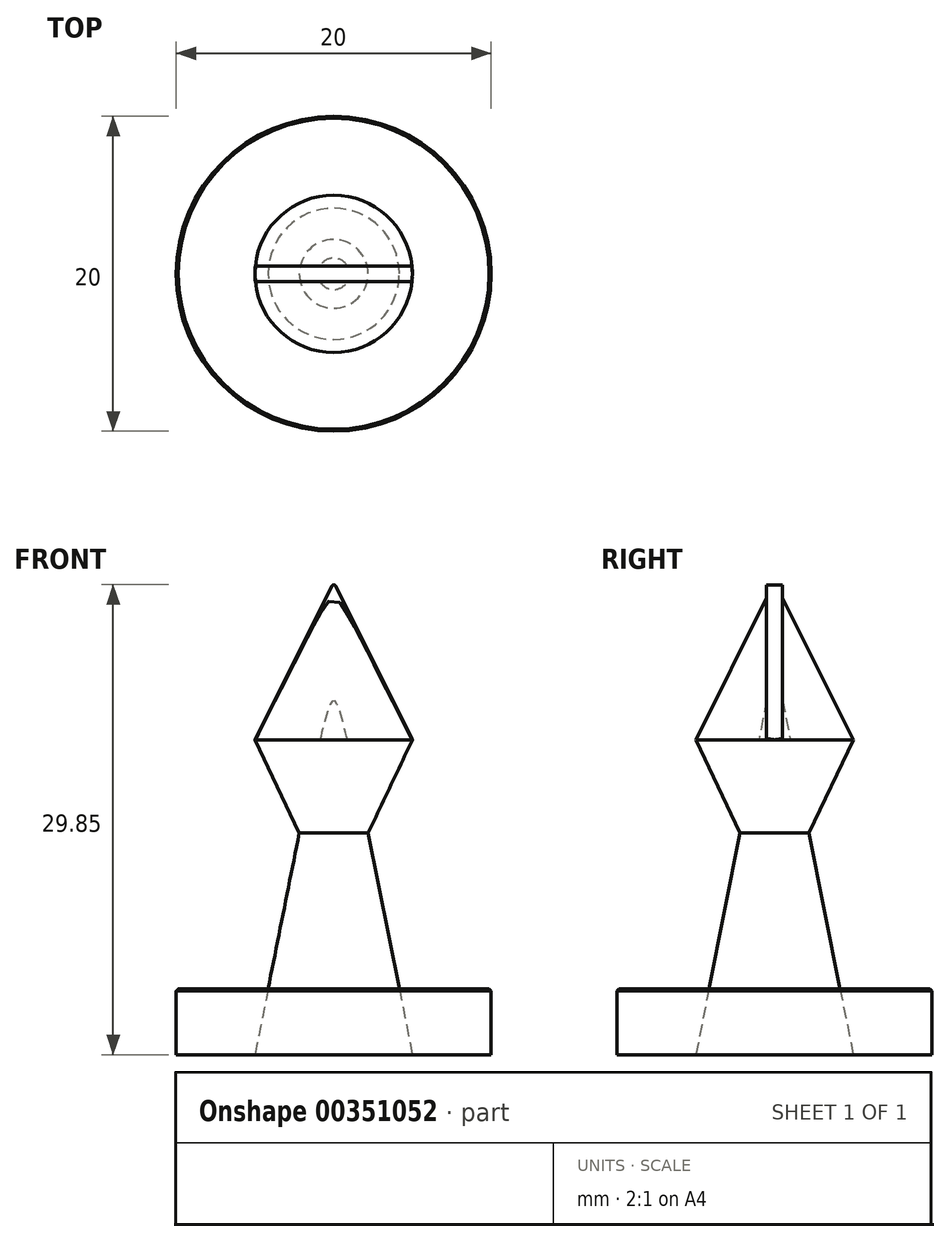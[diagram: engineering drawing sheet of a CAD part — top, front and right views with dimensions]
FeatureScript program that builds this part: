
annotation { "Feature Type Name" : "Feature", "Feature Type Description" : "" }
export const myFeature = defineFeature(function(context is Context, id is Id, definition is map)
    precondition{}
    {
        {
            assignVariable(context, id + "F0", {"name" : "H", "anyValue" : 1});
        }
        {
            assignVariable(context, id + "F1", {"name" : "W", "anyValue" : .5});
        }
        {
            var Q0;
            Q0=qCreatedBy(makeId("Front.planeOp"),FACE);
            var sketch = newSketch(context, id + "F2", { "sketchPlane" : qUnion([Q0])});
            skLineSegment(sketch, "E0", {"start": v(0, 0) * mm, "end": v(0, 30) * mm});
            skPoint(sketch, "E1", {"position": v(0, 20) * mm});
            skPoint(sketch, "E2", {"position": v(0, 25) * mm});
            skLineSegment(sketch, "E3", {"start": v(0, 0) * mm, "end": v(-5, 0) * mm});
            skLineSegment(sketch, "E4", {"start": v(0, 25) * mm, "end": v(-5, 0) * mm});
            skLineSegment(sketch, "E5.bottom", {"start": v(0, 0) * mm, "end": v(-10, 0) * mm});
            skLineSegment(sketch, "E5.top", {"start": v(0, 4.17) * mm, "end": v(-10, 4.17) * mm});
            skLineSegment(sketch, "E5.left", {"start": v(0, 0) * mm, "end": v(0, 4.17) * mm});
            skLineSegment(sketch, "E5.right", {"start": v(-10, 0) * mm, "end": v(-10, 4.17) * mm});
            skLineSegment(sketch, "E6.bottom", {"start": v(-5, 30) * mm, "end": v(5, 30) * mm});
            skLineSegment(sketch, "E6.top", {"start": v(-5, 20) * mm, "end": v(5, 20) * mm});
            skLineSegment(sketch, "E6.left", {"start": v(-5, 30) * mm, "end": v(-5, 20) * mm});
            skLineSegment(sketch, "E6.right", {"start": v(5, 30) * mm, "end": v(5, 20) * mm});
            skLineSegment(sketch, "E7", {"start": v(0, 30) * mm, "end": v(-5, 20) * mm});
            skLineSegment(sketch, "E8", {"start": v(0, 30) * mm, "end": v(5, 20) * mm});
            skLineSegment(sketch, "E9", {"start": v(-5, 20) * mm, "end": v(-2.19, 14.07) * mm});
            skSolve(sketch);
        }
        {
            var Q0;
            {var subQ5=sQuery(id+"F2.wireOp",EDGE,"E5.right");Q0=makeQuery(id+"F2.imprint","IMPRINT",FACE,{"disambiguationData":[TD([[makeQuery(id+"F2.imprint","IMPRINT",EDGE,{"derivedFrom":subQ5}),-1.0]])]});}
            var Q1;
            {var subQ5=sQuery(id+"F2.wireOp",EDGE,"E5.left");Q1=makeQuery(id+"F2.imprint","IMPRINT",FACE,{"disambiguationData":[TD([[makeQuery(id+"F2.imprint","IMPRINT",EDGE,{"derivedFrom":subQ5}),1.0]])]});}
            var Q2;
            {var subQ3=sQuery(id+"F2.wireOp",EDGE,"E6.top");var subQ5=sQuery(id+"F2.wireOp",EDGE,"E4");var subQ6=makeQuery(id+"F2.imprint","INTERSECT",VERTEX,{"derivedFrom":[subQ5,subQ3]});Q2=makeQuery(id+"F2.imprint","IMPRINT",FACE,{"disambiguationData":[TD([[makeQuery(id+"F2.imprint","IMPRINT",EDGE,{"disambiguationData":[TD([[subQ6,-1.0]])],"derivedFrom":subQ5}),1.0]])]});}
            var Q3;
            {var subQ0=sQuery(id+"F2.wireOp",EDGE,"E9");Q3=makeQuery(id+"F2.imprint","IMPRINT",FACE,{"disambiguationData":[TD([[makeQuery(id+"F2.imprint","IMPRINT",EDGE,{"derivedFrom":subQ0}),1.0]])]});}
            var Q4;
            {var subQ0=sQuery(id+"F2.wireOp",EDGE,"E7");Q4=makeQuery(id+"F2.imprint","IMPRINT",FACE,{"disambiguationData":[TD([[makeQuery(id+"F2.imprint","IMPRINT",EDGE,{"derivedFrom":subQ0}),1.0]])]});}
            var Q5;
            Q5=sQuery(id+"F2.wireOp",EDGE,"E0");
            revolve(context, id + "F3", {"entities" : qUnion([Q0, Q1, Q2, Q3, Q4]), "axis" : qUnion([Q5]), "revolveType" : RevolveType.FULL});
        }
        {
            var Q0;
            {var subQ0=sQuery(id+"F2.wireOp",EDGE,"E7");Q0=makeQuery(id+"F2.imprint","IMPRINT",FACE,{"disambiguationData":[TD([[makeQuery(id+"F2.imprint","IMPRINT",EDGE,{"derivedFrom":subQ0}),1.0]])]});}
            var Q1;
            {var subQ0=sQuery(id+"F2.wireOp",EDGE,"E4");var subQ1=sQuery(id+"F2.wireOp",EDGE,"E0");var subQ2=makeQuery(id+"F2.imprint","INTERSECT",VERTEX,{"derivedFrom":[subQ1,subQ0]});Q1=makeQuery(id+"F2.imprint","IMPRINT",FACE,{"disambiguationData":[TD([[makeQuery(id+"F2.imprint","IMPRINT",EDGE,{"disambiguationData":[TD([[subQ2,1.0]])],"derivedFrom":subQ1}),1.0]])]});}
            var Q2;
            {var subQ4=sQuery(id+"F2.wireOp",EDGE,"E8");Q2=makeQuery(id+"F2.imprint","IMPRINT",FACE,{"disambiguationData":[TD([[makeQuery(id+"F2.imprint","IMPRINT",EDGE,{"derivedFrom":subQ4}),-1.0]])]});}
            extrude(context, id + "F4", {"entities" : qUnion([Q0, Q1, Q2]), "operationType" : NewBodyOperationType.ADD, "depth" : (getVariable(context, 'H') / 2) * mm, "hasSecondDirection" : true, "secondDirectionOppositeDirection" : true, "secondDirectionDepth" : (getVariable(context, 'H') / 2) * mm});
        }
        {
            var Q0;
            Q0=makeQuery(id+"F3.opRevolve","SWEPT_EDGE",EDGE,{"disambiguationData":[OSD([sQuery(id+"F2.wireOp",EDGE,"E5.top"),sQuery(id+"F2.wireOp",EDGE,"E5.right")])]});
            chamfer(context, id + "F5", {"entities" : qUnion([Q0]), "width" : (getVariable(context, 'W') / 4) * mm, "tangentPropagation" : true});
        }
        {
            var Q0;
            Q0=makeQuery(id+"F4.opExtrude","SWEPT_EDGE",EDGE,{"disambiguationData":[OSD([sQuery(id+"F2.wireOp",EDGE,"E0"),sQuery(id+"F2.wireOp",EDGE,"E6.bottom"),sQuery(id+"F2.wireOp",EDGE,"E7"),sQuery(id+"F2.wireOp",EDGE,"E8")])]});
            var Q1;
            Q1=makeQuery(id+"F4.opExtrude","SWEPT_EDGE",EDGE,{"disambiguationData":[OSD([sQuery(id+"F2.wireOp",EDGE,"E6.top"),sQuery(id+"F2.wireOp",EDGE,"E6.right"),sQuery(id+"F2.wireOp",EDGE,"E8")])]});
            var Q2;
            Q2=makeQuery(id+"F4.opExtrude","SWEPT_EDGE",EDGE,{"disambiguationData":[OSD([sQuery(id+"F2.wireOp",EDGE,"E6.top"),sQuery(id+"F2.wireOp",EDGE,"E6.left"),sQuery(id+"F2.wireOp",EDGE,"E7")])]});
            fillet(context, id + "F6", {"entities" : qUnion([Q0, Q1, Q2]), "radius" : (getVariable(context, 'W') / 4) * mm, "tangentPropagation" : true, "allowEdgeOverflow" : false});
        }
    });
